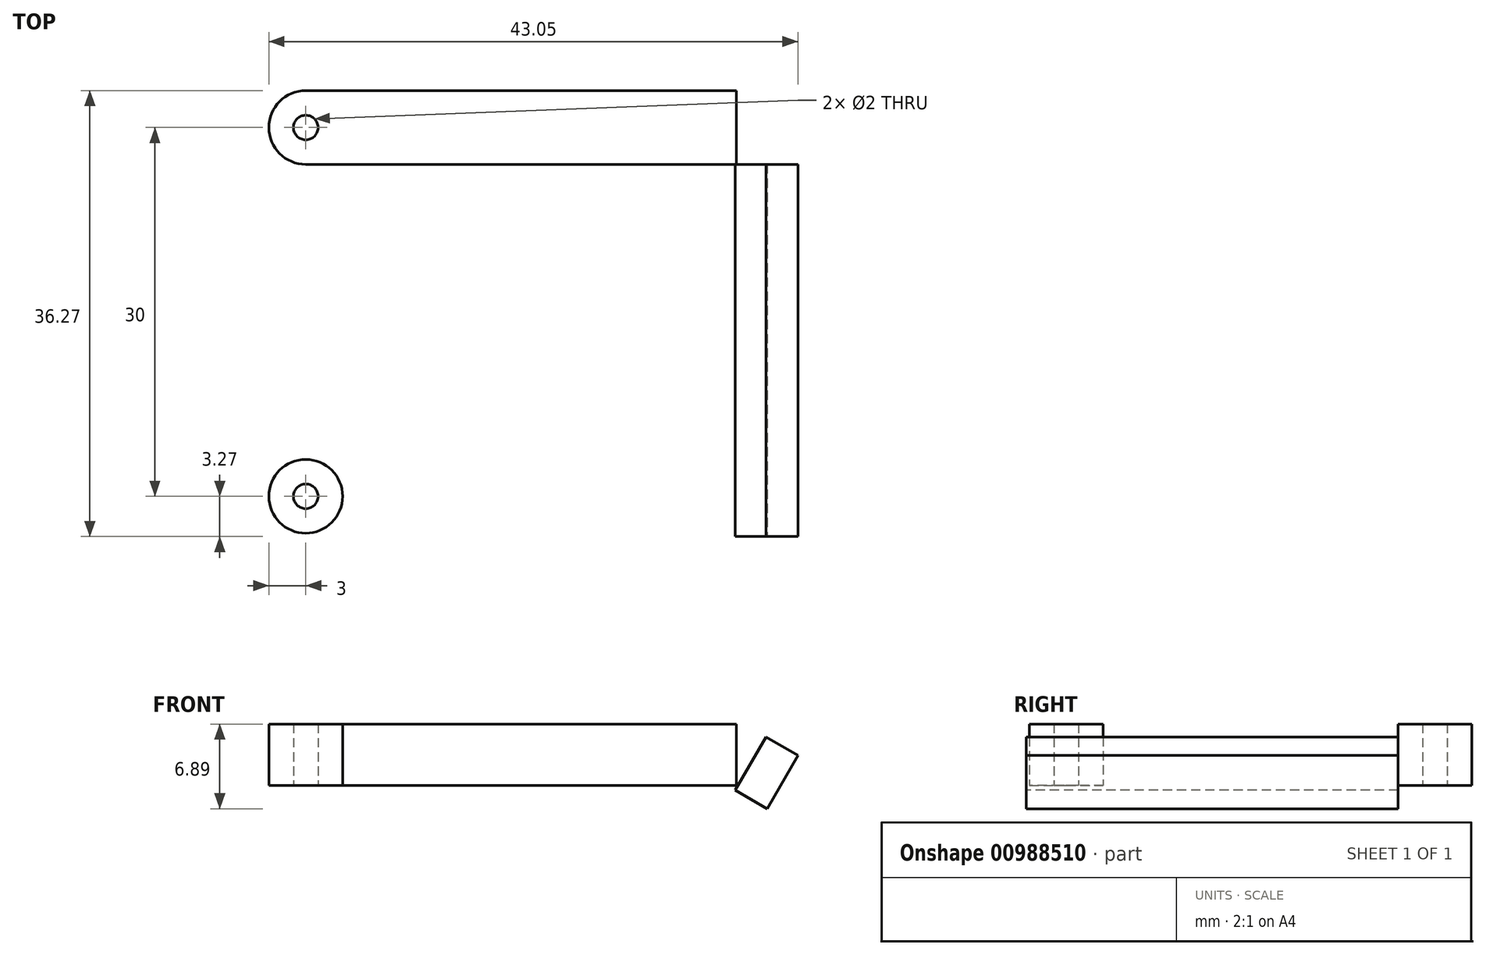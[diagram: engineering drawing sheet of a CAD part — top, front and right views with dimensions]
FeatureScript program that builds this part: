
annotation { "Feature Type Name" : "Feature", "Feature Type Description" : "" }
export const myFeature = defineFeature(function(context is Context, id is Id, definition is map)
    precondition{}
    {
        {
            var Q0;
            Q0=qCreatedBy(makeId("Top.planeOp"),FACE);
            var sketch = newSketch(context, id + "F0", { "sketchPlane" : qUnion([Q0])});
            skCircle(sketch, "E0", {"center": v(-12, 15) * mm, "radius": 1 * mm});
            skCircle(sketch, "E1", {"center": v(-12, -15) * mm, "radius": 1 * mm});
            skCircle(sketch, "E2.0", {"center": v(-12, 15) * mm, "radius": 3 * mm});
            skCircle(sketch, "E3.0", {"center": v(-12, -15) * mm, "radius": 3 * mm});
            skLineSegment(sketch, "E4.bottom", {"start": v(-12, 18) * mm, "end": v(23.05, 18) * mm});
            skLineSegment(sketch, "E4.top", {"start": v(-12, 12) * mm, "end": v(23.05, 12) * mm});
            skLineSegment(sketch, "E4.left", {"start": v(-12, 18) * mm, "end": v(-12, 12) * mm});
            skLineSegment(sketch, "E4.right", {"start": v(23.05, 18) * mm, "end": v(23.05, 12) * mm});
            skSolve(sketch);
        }
        {
            var Q0;
            Q0 = qSketchRegion(id + "F0", true);
            extrude(context, id + "F1", {"entities" : qUnion([Q0]), "depth" : 5 * mm, "offsetDistance" : 25 * mm});
        }
        {
            var Q0;
            Q0=makeQuery(id+"F1.opExtrude","SWEPT_FACE",FACE,{"disambiguationData":[OSD([sQuery(id+"F0.wireOp",EDGE,"E4.right")])]});
            var sketch = newSketch(context, id + "F2", { "sketchPlane" : qUnion([Q0])});
            skLineSegment(sketch, "E5.bottom", {"start": v(18, 5) * mm, "end": v(-18.27, 5) * mm});
            skLineSegment(sketch, "E5.top", {"start": v(18, 0) * mm, "end": v(-18.27, 0) * mm});
            skLineSegment(sketch, "E5.left", {"start": v(18, 5) * mm, "end": v(18, 0) * mm});
            skLineSegment(sketch, "E5.right", {"start": v(-18.27, 5) * mm, "end": v(-18.27, 0) * mm});
            skSolve(sketch);
        }
        {
            var Q0;
            Q0=qCreatedBy(makeId("Top.planeOp"),FACE);
            var sketch = newSketch(context, id + "F3", { "sketchPlane" : qUnion([Q0])});
            skLineSegment(sketch, "E6", {"start": v(22.28, 17.88) * mm, "end": v(22.28, -25.64) * mm, "construction": true});
            skSolve(sketch);
        }
        {
            var Q0;
            {var subQ2=sQuery(id+"F2.wireOp",EDGE,"E5.right");Q0=makeQuery(id+"F2.imprint","IMPRINT",FACE,{"disambiguationData":[TD([[makeQuery(id+"F2.imprint","IMPRINT",EDGE,{"derivedFrom":subQ2}),1.0]])]});}
            extrude(context, id + "F4", {"entities" : qUnion([Q0]), "depth" : 3 * mm, "offsetDistance" : 25 * mm});
        }
        {
            var Q0;
            Q0=makeQuery(id+"F4.opExtrude","SWEPT_BODY",BODY,{"disambiguationData":[OSD([sQuery(id+"F0.wireOp",EDGE,"E4.top"),sQuery(id+"F0.wireOp",EDGE,"E4.right"),sQuery(id+"F2.wireOp",EDGE,"E5.bottom"),sQuery(id+"F2.wireOp",EDGE,"E5.top"),sQuery(id+"F2.wireOp",EDGE,"E5.right")])]});
            var Q1;
            Q1=sQuery(id+"F3.wireOp",EDGE,"E6");
            transform(context, id + "F5", {"entities" : qUnion([Q0]), "transformType" : TransformType.ROTATION, "transformAxis" : qUnion([Q1]), "angle" : 30 * degree, "oppositeDirection" : true, "makeCopy" : false});
        }
    });
